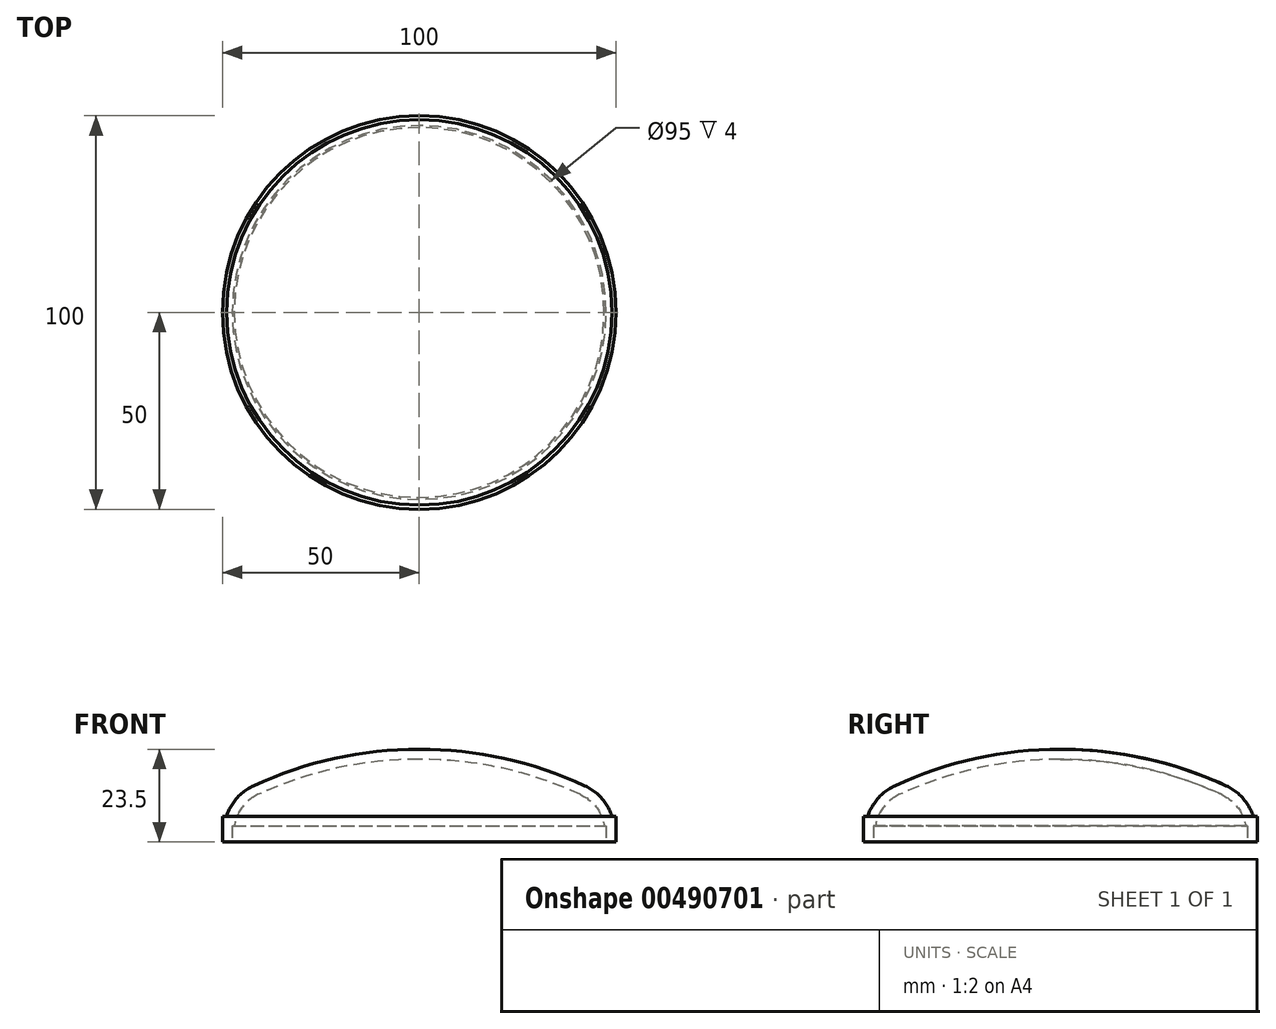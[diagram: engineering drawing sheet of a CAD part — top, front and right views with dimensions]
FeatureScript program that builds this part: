
annotation { "Feature Type Name" : "Feature", "Feature Type Description" : "" }
export const myFeature = defineFeature(function(context is Context, id is Id, definition is map)
    precondition{}
    {
        {
            var Q0;
            Q0=qCreatedBy(makeId("Right.planeOp"),FACE);
            var sketch = newSketch(context, id + "F0", { "sketchPlane" : qUnion([Q0])});
            skLineSegment(sketch, "E0", {"start": v(0, 0) * mm, "end": v(41, 0) * mm, "construction": true});
            skLineSegment(sketch, "E1", {"start": v(0, 0) * mm, "end": v(0, 9) * mm, "construction": true});
            skLineSegment(sketch, "E2", {"start": v(0, 0) * mm, "end": v(0, -8) * mm, "construction": true});
            skLineSegment(sketch, "E3", {"start": v(0, -8) * mm, "end": v(47, -8) * mm, "construction": true});
            skLineSegment(sketch, "E4", {"start": v(0, 0) * mm, "end": v(-41, 0) * mm, "construction": true});
            skArc(sketch, "E5", {"start": v(41, 0) * mm, "mid": v(20.99, 6.72) * mm, "end": v(0, 9) * mm});
            skArc(sketch, "E6", {"start": v(41, 0) * mm, "mid": v(45.01, -3.24) * mm, "end": v(47, -8) * mm});
            skPoint(sketch, "E7.endSnap0", {"position": v(0, 4.5) * mm});
            skPoint(sketch, "E8.orphan", {"position": v(0, 13.16) * mm});
            skLineSegment(sketch, "E9.0", {"start": v(0, -12) * mm, "end": v(47.5, -12) * mm, "construction": true});
            skLineSegment(sketch, "E10.0", {"start": v(47.5, -8) * mm, "end": v(47.5, -12) * mm});
            skLineSegment(sketch, "E11", {"start": v(47, -8) * mm, "end": v(47.5, -8) * mm});
            skArc(sketch, "E12.0", {"start": v(42.05, 2.27) * mm, "mid": v(21.52, 9.17) * mm, "end": v(0, 11.5) * mm});
            skArc(sketch, "E12.1", {"start": v(42.05, 2.27) * mm, "mid": v(46.32, -0.9) * mm, "end": v(48.97, -5.5) * mm});
            skLineSegment(sketch, "E12.2", {"start": v(48.97, -5.5) * mm, "end": v(50, -5.5) * mm});
            skLineSegment(sketch, "E12.3", {"start": v(50, -5.5) * mm, "end": v(50, -12) * mm});
            skLineSegment(sketch, "E13", {"start": v(0, 11.5) * mm, "end": v(0, 9) * mm});
            skLineSegment(sketch, "E14", {"start": v(47.5, -12) * mm, "end": v(50, -12) * mm});
            skSolve(sketch);
        }
        {
            var Q0;
            Q0=makeQuery(id+"F0.imprint","IMPRINT",FACE,{"disambiguationData":[TD([[makeQuery(id+"F0.imprint","IMPRINT",EDGE,{"derivedFrom":sQuery(id+"F0.wireOp",EDGE,"E5")}),-1.0]])]});
            var Q1;
            Q1=sQuery(id+"F0.wireOp",EDGE,"E1");
            revolve(context, id + "F1", {"entities" : qUnion([Q0]), "axis" : qUnion([Q1]), "revolveType" : RevolveType.FULL});
        }
    });
